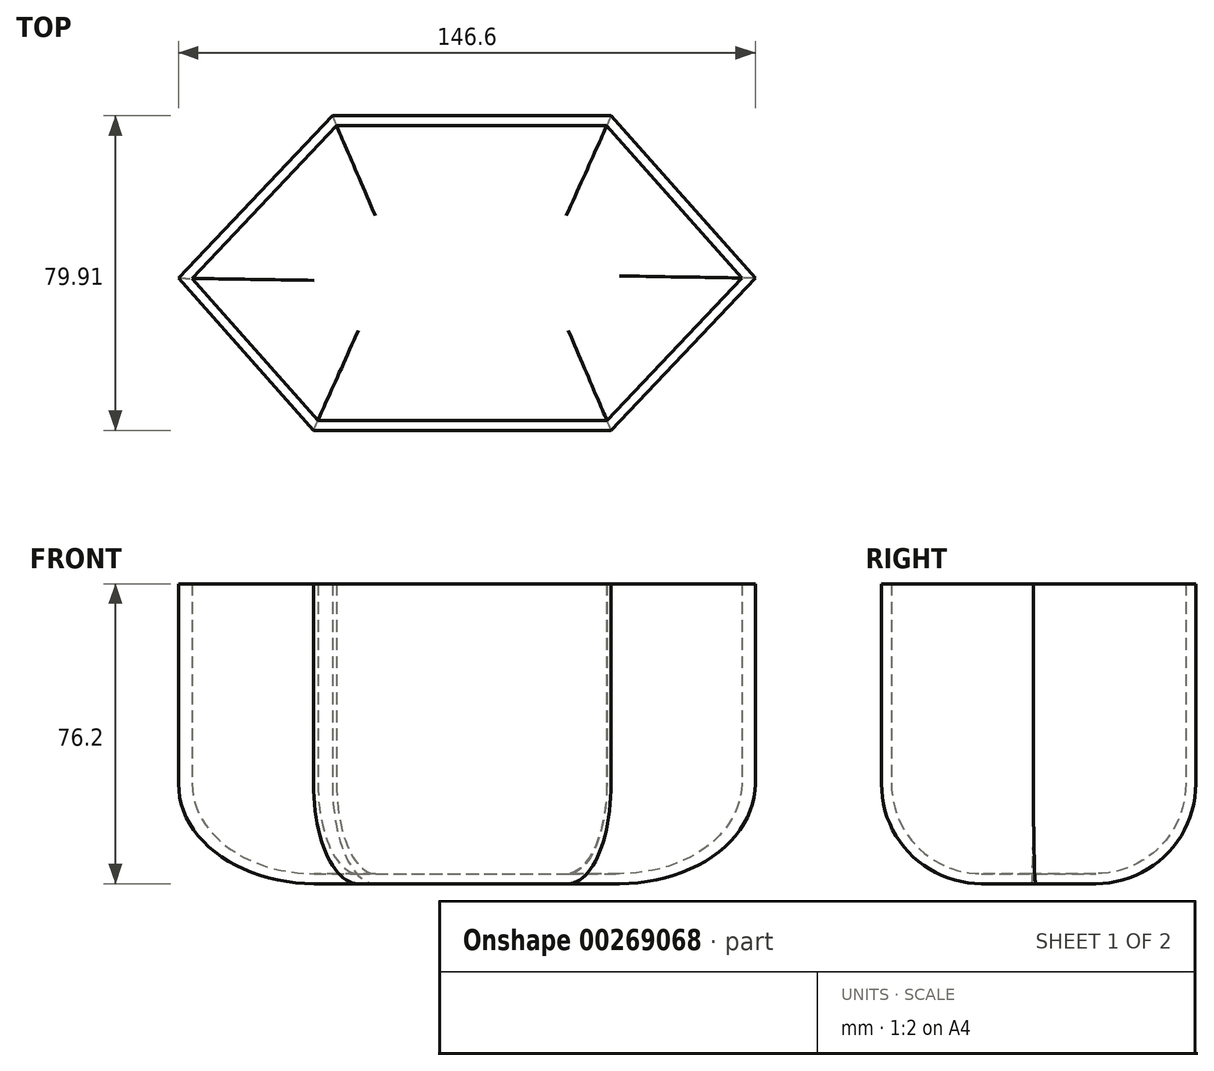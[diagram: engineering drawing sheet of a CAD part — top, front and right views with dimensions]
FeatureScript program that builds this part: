
annotation { "Feature Type Name" : "Feature", "Feature Type Description" : "" }
export const myFeature = defineFeature(function(context is Context, id is Id, definition is map)
    precondition{}
    {
        {
            var Q0;
            Q0=qCreatedBy(makeId("Top.planeOp"),FACE);
            var sketch = newSketch(context, id + "F0", { "sketchPlane" : qUnion([Q0])});
            skLineSegment(sketch, "E0", {"start": v(-70.74, 0) * mm, "end": v(-31.62, 41.26) * mm});
            skLineSegment(sketch, "E1", {"start": v(-31.62, 41.26) * mm, "end": v(39.22, 41.26) * mm});
            skLineSegment(sketch, "E2", {"start": v(39.22, 41.26) * mm, "end": v(75.86, 0) * mm});
            skLineSegment(sketch, "E3", {"start": v(75.86, 0) * mm, "end": v(39.22, -38.65) * mm});
            skLineSegment(sketch, "E4", {"start": v(39.22, -38.65) * mm, "end": v(-36.42, -38.65) * mm});
            skLineSegment(sketch, "E5", {"start": v(-36.42, -38.65) * mm, "end": v(-70.74, 0) * mm});
            skSolve(sketch);
        }
        {
            var Q0;
            Q0=makeQuery(id+"F0.imprint","IMPRINT",FACE,{"disambiguationData":[TD([[makeQuery(id+"F0.imprint","IMPRINT",EDGE,{"derivedFrom":sQuery(id+"F0.wireOp",EDGE,"E0")}),-1.0]])]});
            extrude(context, id + "F1", {"entities" : qUnion([Q0]), "depth" : 76.2 * mm});
        }
        {
            var Q0;
            Q0=makeQuery(id+"F1.opExtrude","CAP_FACE",FACE,{"disambiguationData":[OSD([sQuery(id+"F0.wireOp",EDGE,"E0"),sQuery(id+"F0.wireOp",EDGE,"E1"),sQuery(id+"F0.wireOp",EDGE,"E2"),sQuery(id+"F0.wireOp",EDGE,"E3"),sQuery(id+"F0.wireOp",EDGE,"E4"),sQuery(id+"F0.wireOp",EDGE,"E5")])],"isStart":true});
            fillet(context, id + "F2", {"entities" : qUnion([Q0]), "radius" : 25.4 * mm, "tangentPropagation" : true, "allowEdgeOverflow" : false});
        }
        {
            var Q0;
            Q0=makeQuery(id+"F1.opExtrude","CAP_FACE",FACE,{"disambiguationData":[OSD([sQuery(id+"F0.wireOp",EDGE,"E0"),sQuery(id+"F0.wireOp",EDGE,"E1"),sQuery(id+"F0.wireOp",EDGE,"E2"),sQuery(id+"F0.wireOp",EDGE,"E3"),sQuery(id+"F0.wireOp",EDGE,"E4"),sQuery(id+"F0.wireOp",EDGE,"E5")])],"isStart":false});
            shell(context, id + "F3", {"entities" : qUnion([Q0]), "thickness" : 2.54 * mm});
        }
    });
